# Revit family: METALFIRE_CITIZEN_MF_WHE_1S
name_source: partatom
category: Mechanical Equipment
revit_build: Autodesk Revit 2017 (Build: 20160225_1515(x64)
units: mm (PartAtom-declared; Revit-internal decimal feet)

## family parameters
Always vertical = Yes
Cut with Voids When Loaded = No
Host = Wall
OmniClass Number = 23.75.00.00
OmniClass Title = Climate Control (HVAC)
Part Type = Normal
Room Calculation Point = Yes
Round Connector Dimension = Use Diameter
Shared = No

## types (4) — shared parameters
BIM BADGE = https://bim.archiproducts.com
Description = The Citizen is a compact closed wood-fired fireplace with hinged door.
FINISHING MATERIAL = Black painted vermiculite plates - Metalfire
FRAME MATERIAL = Iron - Metalfire
MATERIAL DESCRIPTION = Iron, galvanized steel and vermiculite plates
Manufacturer = Metalfire
Model = Citizen
OVERALL DEPTH = 488 mm
PRODUCT SHEET = https://www.archiproducts.com
TECHNICAL SHEET = https://www.metalfire.eu
URL = https://www.metalfire.eu

## per-type parameters (varying)
| type | CO EMISSION | EFFICIENCY | ENERGY EFFICIENCY CLASS | FINE DUST EMISSION | HEIGHT | OUTPUT | OVERALL HEIGHT | OVERALL WIDTH | PRODUCT CODE | SMOKE EXHAUST | WEIGHT | WIDTH |
| 700 x 600 mm | 0.09% | 80.00% | A+ | 25 mg/Nm3 | 602 mm | 12.2 kW | 1098 mm | 823 mm | MF 700-60 WHE 1S | Ø150/180 mm | 195.00 kg | 702 mm |
| 900 x 450 mm | 0.08% | 78.00% | A | 28 mg/Nm3 | 452 mm | 12.8 kW | 948 mm | 1023 mm | MF 900-45 WHE 1S | Ø150/180 mm | 200.00 kg | 902 mm |
| 900 x 600 mm | 0.10% | 79.00% | A+ | 26 mg/Nm3 | 602 mm | 15.0 kW | 1096 mm | 1023 mm | MF 900-60 WHE 1S | Ø180 mm | 230.00 kg | 902 mm |
| 1050 x 450 mm | 0.09% | 79.00% | A+ | 23 mg/Nm3 | 452 mm | 13.4 kW | 948 mm | 1173 mm | MF 1050-45 WHE 1S | Ø180 mm | 230.00 kg | 1052 mm |

## geometry (parser evidence)
native form markers: Sweep x4
no freeform markers — native parametric forms only
